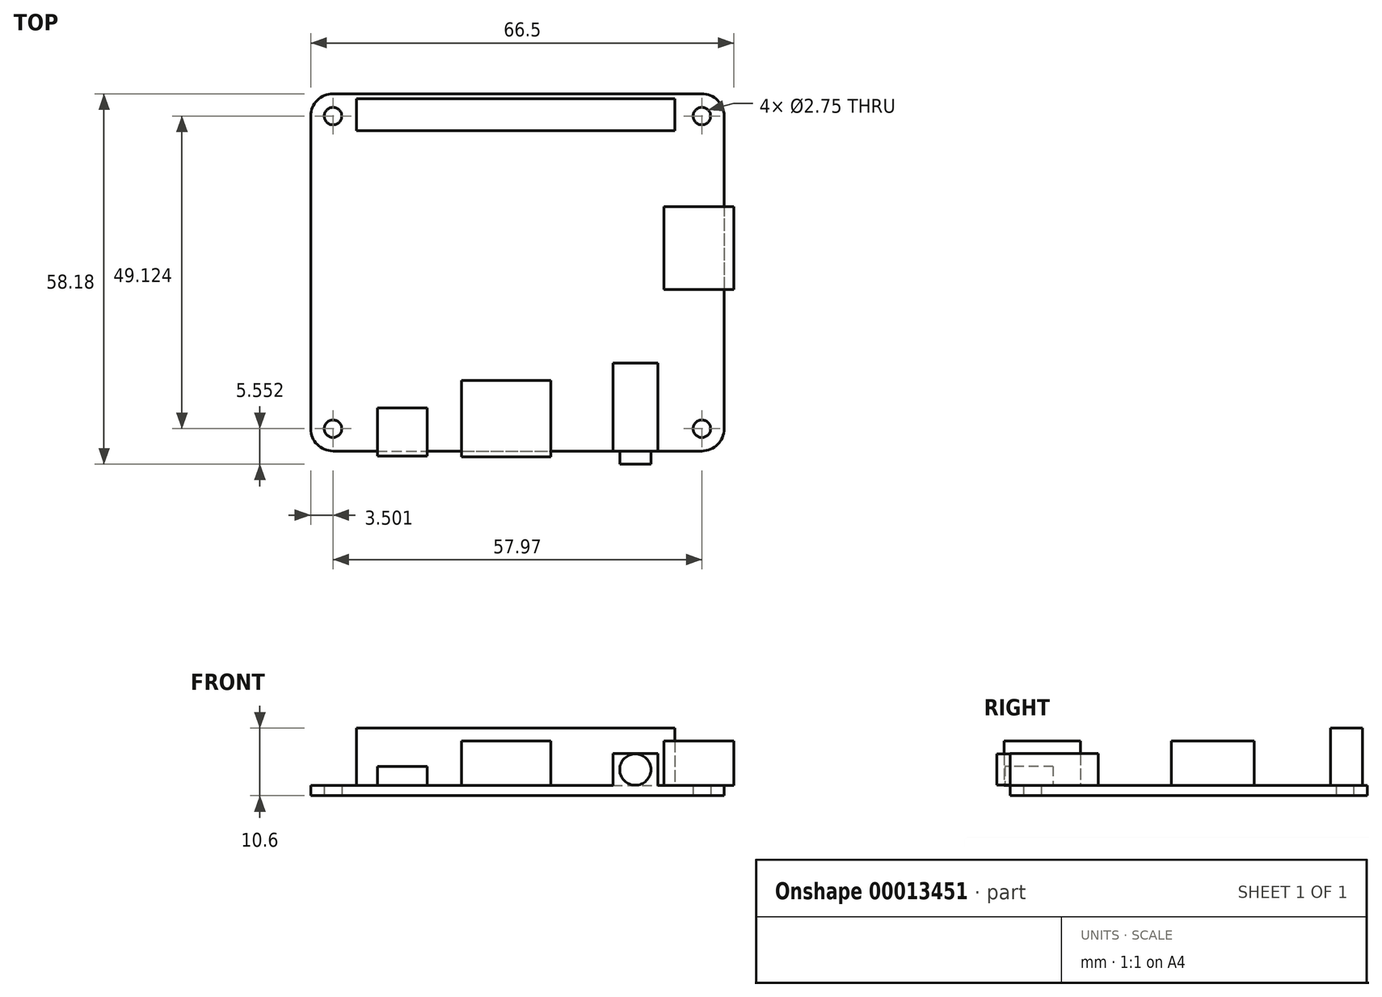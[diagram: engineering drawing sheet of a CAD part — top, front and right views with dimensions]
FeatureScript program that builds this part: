
annotation { "Feature Type Name" : "Feature", "Feature Type Description" : "" }
export const myFeature = defineFeature(function(context is Context, id is Id, definition is map)
    precondition{}
    {
        {
            var Q0;
            Q0=qCreatedBy(makeId("Top.planeOp"),FACE);
            var sketch = newSketch(context, id + "F0", { "sketchPlane" : qUnion([Q0])});
            skLineSegment(sketch, "E0.bottom", {"start": v(-31.28, 47.32) * mm, "end": v(26.7, 47.32) * mm});
            skLineSegment(sketch, "E0.top", {"start": v(-31.28, -8.8) * mm, "end": v(26.7, -8.8) * mm});
            skLineSegment(sketch, "E0.left", {"start": v(-34.78, 43.82) * mm, "end": v(-34.78, -5.3) * mm});
            skLineSegment(sketch, "E0.right", {"start": v(30.2, 43.82) * mm, "end": v(30.2, -5.3) * mm});
            skPoint(sketch, "E1.visualSharp", {"position": v(-34.78, -8.8) * mm});
            skArc(sketch, "E1.filletArc", {"start": v(-34.78, -5.3) * mm, "mid": v(-33.75, -7.78) * mm, "end": v(-31.28, -8.8) * mm});
            skCircle(sketch, "E2", {"center": v(-31.28, -5.3) * mm, "radius": 1.38 * mm});
            skPoint(sketch, "E3.visualSharp", {"position": v(-34.78, 47.32) * mm});
            skArc(sketch, "E3.filletArc", {"start": v(-31.28, 47.32) * mm, "mid": v(-33.75, 46.3) * mm, "end": v(-34.78, 43.82) * mm});
            skPoint(sketch, "E4.visualSharp", {"position": v(30.2, 47.32) * mm});
            skArc(sketch, "E4.filletArc", {"start": v(30.2, 43.82) * mm, "mid": v(29.17, 46.3) * mm, "end": v(26.7, 47.32) * mm});
            skPoint(sketch, "E5.visualSharp", {"position": v(30.2, -8.8) * mm});
            skArc(sketch, "E5.filletArc", {"start": v(26.7, -8.8) * mm, "mid": v(29.17, -7.78) * mm, "end": v(30.2, -5.3) * mm});
            skCircle(sketch, "E6", {"center": v(-31.28, 43.82) * mm, "radius": 1.38 * mm});
            skCircle(sketch, "E7", {"center": v(26.7, 43.82) * mm, "radius": 1.38 * mm});
            skCircle(sketch, "E8", {"center": v(26.7, -5.3) * mm, "radius": 1.38 * mm});
            skSolve(sketch);
        }
        {
            var Q0;
            Q0=makeQuery(id+"F0.imprint","IMPRINT",FACE,{"disambiguationData":[TD([[makeQuery(id+"F0.imprint","IMPRINT",EDGE,{"derivedFrom":sQuery(id+"F0.wireOp",EDGE,"E0.bottom")}),-1.0]])]});
            extrude(context, id + "F1", {"entities" : qUnion([Q0]), "depth" : 1.6 * mm});
        }
        {
            var Q0;
            Q0=makeQuery(id+"F1.opExtrude","CAP_FACE",FACE,{"disambiguationData":[OSD([sQuery(id+"F0.wireOp",EDGE,"E0.bottom"),sQuery(id+"F0.wireOp",EDGE,"E0.top"),sQuery(id+"F0.wireOp",EDGE,"E0.left"),sQuery(id+"F0.wireOp",EDGE,"E0.right"),sQuery(id+"F0.wireOp",EDGE,"E1.filletArc"),sQuery(id+"F0.wireOp",EDGE,"E2"),sQuery(id+"F0.wireOp",EDGE,"E3.filletArc"),sQuery(id+"F0.wireOp",EDGE,"E4.filletArc"),sQuery(id+"F0.wireOp",EDGE,"E5.filletArc"),sQuery(id+"F0.wireOp",EDGE,"E6"),sQuery(id+"F0.wireOp",EDGE,"E7"),sQuery(id+"F0.wireOp",EDGE,"E8")])],"isStart":false});
            var sketch = newSketch(context, id + "F2", { "sketchPlane" : qUnion([Q0])});
            skLineSegment(sketch, "E9.bottom", {"start": v(-11.08, 2.26) * mm, "end": v(2.92, 2.26) * mm});
            skLineSegment(sketch, "E9.top", {"start": v(-11.08, -9.74) * mm, "end": v(2.92, -9.74) * mm});
            skLineSegment(sketch, "E9.left", {"start": v(-11.08, 2.26) * mm, "end": v(-11.08, -9.74) * mm});
            skLineSegment(sketch, "E9.right", {"start": v(2.92, 2.26) * mm, "end": v(2.92, -9.74) * mm});
            skSolve(sketch);
        }
        {
            var Q0;
            Q0=qSketchRegion(id+"F2",true);
            extrude(context, id + "F3", {"entities" : qUnion([Q0]), "operationType" : NewBodyOperationType.ADD, "depth" : 7 * mm});
        }
        {
            var Q0;
            Q0=makeQuery(id+"F1.opExtrude","CAP_FACE",FACE,{"disambiguationData":[OSD([sQuery(id+"F0.wireOp",EDGE,"E0.bottom"),sQuery(id+"F0.wireOp",EDGE,"E0.top"),sQuery(id+"F0.wireOp",EDGE,"E0.left"),sQuery(id+"F0.wireOp",EDGE,"E0.right"),sQuery(id+"F0.wireOp",EDGE,"E1.filletArc"),sQuery(id+"F0.wireOp",EDGE,"E2"),sQuery(id+"F0.wireOp",EDGE,"E3.filletArc"),sQuery(id+"F0.wireOp",EDGE,"E4.filletArc"),sQuery(id+"F0.wireOp",EDGE,"E5.filletArc"),sQuery(id+"F0.wireOp",EDGE,"E6"),sQuery(id+"F0.wireOp",EDGE,"E7"),sQuery(id+"F0.wireOp",EDGE,"E8")])],"isStart":false});
            var sketch = newSketch(context, id + "F4", { "sketchPlane" : qUnion([Q0])});
            skLineSegment(sketch, "E10.bottom", {"start": v(-27.57, 46.55) * mm, "end": v(22.43, 46.55) * mm});
            skLineSegment(sketch, "E10.top", {"start": v(-27.57, 41.55) * mm, "end": v(22.43, 41.55) * mm});
            skLineSegment(sketch, "E10.left", {"start": v(-27.57, 46.55) * mm, "end": v(-27.57, 41.55) * mm});
            skLineSegment(sketch, "E10.right", {"start": v(22.43, 46.55) * mm, "end": v(22.43, 41.55) * mm});
            skSolve(sketch);
        }
        {
            var Q0;
            Q0=qSketchRegion(id+"F4",true);
            extrude(context, id + "F5", {"entities" : qUnion([Q0]), "operationType" : NewBodyOperationType.ADD, "depth" : 9 * mm});
        }
        {
            var Q0;
            Q0=makeQuery(id+"F1.opExtrude","CAP_FACE",FACE,{"disambiguationData":[OSD([sQuery(id+"F0.wireOp",EDGE,"E0.bottom"),sQuery(id+"F0.wireOp",EDGE,"E0.top"),sQuery(id+"F0.wireOp",EDGE,"E0.left"),sQuery(id+"F0.wireOp",EDGE,"E0.right"),sQuery(id+"F0.wireOp",EDGE,"E1.filletArc"),sQuery(id+"F0.wireOp",EDGE,"E2"),sQuery(id+"F0.wireOp",EDGE,"E3.filletArc"),sQuery(id+"F0.wireOp",EDGE,"E4.filletArc"),sQuery(id+"F0.wireOp",EDGE,"E5.filletArc"),sQuery(id+"F0.wireOp",EDGE,"E6"),sQuery(id+"F0.wireOp",EDGE,"E7"),sQuery(id+"F0.wireOp",EDGE,"E8")])],"isStart":false});
            var sketch = newSketch(context, id + "F6", { "sketchPlane" : qUnion([Q0])});
            skLineSegment(sketch, "E11.bottom", {"start": v(31.72, 29.55) * mm, "end": v(20.72, 29.55) * mm});
            skLineSegment(sketch, "E11.top", {"start": v(31.72, 16.55) * mm, "end": v(20.72, 16.55) * mm});
            skLineSegment(sketch, "E11.left", {"start": v(31.72, 29.55) * mm, "end": v(31.72, 16.55) * mm});
            skLineSegment(sketch, "E11.right", {"start": v(20.72, 29.55) * mm, "end": v(20.72, 16.55) * mm});
            skSolve(sketch);
        }
        {
            var Q0;
            Q0=qSketchRegion(id+"F6",true);
            extrude(context, id + "F7", {"entities" : qUnion([Q0]), "operationType" : NewBodyOperationType.ADD, "depth" : 7 * mm});
        }
        {
            var Q0;
            Q0=makeQuery(id+"F1.opExtrude","CAP_FACE",FACE,{"disambiguationData":[OSD([sQuery(id+"F0.wireOp",EDGE,"E0.bottom"),sQuery(id+"F0.wireOp",EDGE,"E0.top"),sQuery(id+"F0.wireOp",EDGE,"E0.left"),sQuery(id+"F0.wireOp",EDGE,"E0.right"),sQuery(id+"F0.wireOp",EDGE,"E1.filletArc"),sQuery(id+"F0.wireOp",EDGE,"E2"),sQuery(id+"F0.wireOp",EDGE,"E3.filletArc"),sQuery(id+"F0.wireOp",EDGE,"E4.filletArc"),sQuery(id+"F0.wireOp",EDGE,"E5.filletArc"),sQuery(id+"F0.wireOp",EDGE,"E6"),sQuery(id+"F0.wireOp",EDGE,"E7"),sQuery(id+"F0.wireOp",EDGE,"E8")])],"isStart":false});
            var sketch = newSketch(context, id + "F8", { "sketchPlane" : qUnion([Q0])});
            skLineSegment(sketch, "E12.bottom", {"start": v(-24.26, -2.05) * mm, "end": v(-16.45, -2.05) * mm});
            skLineSegment(sketch, "E12.top", {"start": v(-24.26, -9.6) * mm, "end": v(-16.45, -9.6) * mm});
            skLineSegment(sketch, "E12.left", {"start": v(-24.26, -2.05) * mm, "end": v(-24.26, -9.6) * mm});
            skLineSegment(sketch, "E12.right", {"start": v(-16.45, -2.05) * mm, "end": v(-16.45, -9.6) * mm});
            skSolve(sketch);
        }
        {
            var Q0;
            Q0=qSketchRegion(id+"F8",true);
            extrude(context, id + "F9", {"entities" : qUnion([Q0]), "operationType" : NewBodyOperationType.ADD, "depth" : 3 * mm});
        }
        {
            var Q0;
            Q0=makeQuery(id+"F1.opExtrude","CAP_FACE",FACE,{"disambiguationData":[OSD([sQuery(id+"F0.wireOp",EDGE,"E0.bottom"),sQuery(id+"F0.wireOp",EDGE,"E0.top"),sQuery(id+"F0.wireOp",EDGE,"E0.left"),sQuery(id+"F0.wireOp",EDGE,"E0.right"),sQuery(id+"F0.wireOp",EDGE,"E1.filletArc"),sQuery(id+"F0.wireOp",EDGE,"E2"),sQuery(id+"F0.wireOp",EDGE,"E3.filletArc"),sQuery(id+"F0.wireOp",EDGE,"E4.filletArc"),sQuery(id+"F0.wireOp",EDGE,"E5.filletArc"),sQuery(id+"F0.wireOp",EDGE,"E6"),sQuery(id+"F0.wireOp",EDGE,"E7"),sQuery(id+"F0.wireOp",EDGE,"E8")])],"isStart":false});
            var sketch = newSketch(context, id + "F10", { "sketchPlane" : qUnion([Q0])});
            skLineSegment(sketch, "E13.bottom", {"start": v(12.7, -8.8) * mm, "end": v(19.76, -8.8) * mm});
            skLineSegment(sketch, "E13.top", {"start": v(12.7, 5.02) * mm, "end": v(19.76, 5.02) * mm});
            skLineSegment(sketch, "E13.left", {"start": v(12.7, -8.8) * mm, "end": v(12.7, 5.02) * mm});
            skLineSegment(sketch, "E13.right", {"start": v(19.76, -8.8) * mm, "end": v(19.76, 5.02) * mm});
            skSolve(sketch);
        }
        {
            var Q0;
            Q0=qSketchRegion(id+"F10",true);
            extrude(context, id + "F11", {"entities" : qUnion([Q0]), "operationType" : NewBodyOperationType.ADD, "depth" : 5 * mm});
        }
        {
            var Q0;
            Q0=makeQuery(id+"F11.boolean.opBoolean","MERGE",FACE,{"derivedFrom":[makeQuery(id+"F1.opExtrude","SWEPT_FACE",FACE,{"disambiguationData":[OSD([sQuery(id+"F0.wireOp",EDGE,"E0.top")])]}),makeQuery(id+"F11.opExtrude","SWEPT_FACE",FACE,{"disambiguationData":[OSD([sQuery(id+"F10.wireOp",EDGE,"E13.bottom")])]})]});
            var sketch = newSketch(context, id + "F12", { "sketchPlane" : qUnion([Q0])});
            skLineSegment(sketch, "E14", {"start": v(12.7, 1.6) * mm, "end": v(19.76, 1.6) * mm, "construction": true});
            skLineSegment(sketch, "E15", {"start": v(16.23, 1.6) * mm, "end": v(16.23, 6.6) * mm, "construction": true});
            skLineSegment(sketch, "E16", {"start": v(19.76, 4.1) * mm, "end": v(12.7, 4.1) * mm, "construction": true});
            skCircle(sketch, "E17", {"center": v(16.23, 4.1) * mm, "radius": 2.45 * mm});
            skSolve(sketch);
        }
        {
            var Q0;
            Q0=qSketchRegion(id+"F12",true);
            extrude(context, id + "F13", {"entities" : qUnion([Q0]), "operationType" : NewBodyOperationType.ADD, "depth" : 2.05 * mm});
        }
        {
            var Q0;
            Q0=makeQuery(id+"F5.opExtrude","CAP_FACE",FACE,{"disambiguationData":[OSD([sQuery(id+"F4.wireOp",EDGE,"E10.bottom"),sQuery(id+"F4.wireOp",EDGE,"E10.top"),sQuery(id+"F4.wireOp",EDGE,"E10.left"),sQuery(id+"F4.wireOp",EDGE,"E10.right")])],"isStart":false});
            var sketch = newSketch(context, id + "F14", { "sketchPlane" : qUnion([Q0])});
            skLineSegment(sketch, "E18.0", {"start": v(-26.57, 45.55) * mm, "end": v(21.43, 45.55) * mm});
            skLineSegment(sketch, "E18.1", {"start": v(-26.57, 45.55) * mm, "end": v(-26.57, 42.55) * mm});
            skLineSegment(sketch, "E18.2", {"start": v(-26.57, 42.55) * mm, "end": v(21.43, 42.55) * mm});
            skLineSegment(sketch, "E18.3", {"start": v(21.43, 45.55) * mm, "end": v(21.43, 42.55) * mm});
            skSolve(sketch);
        }
        {
            var Q0;
            Q0=makeQuery(id+"F14.imprint","IMPRINT",FACE,{"disambiguationData":[TD([[makeQuery(id+"F14.imprint","IMPRINT",EDGE,{"derivedFrom":sQuery(id+"F14.wireOp",EDGE,"E18.0")}),1.0]])]});
            extrude(context, id + "F15", {"entities" : qUnion([Q0]), "operationType" : NewBodyOperationType.ADD, "oppositeDirection" : true, "depth" : 5 * mm});
        }
    });
